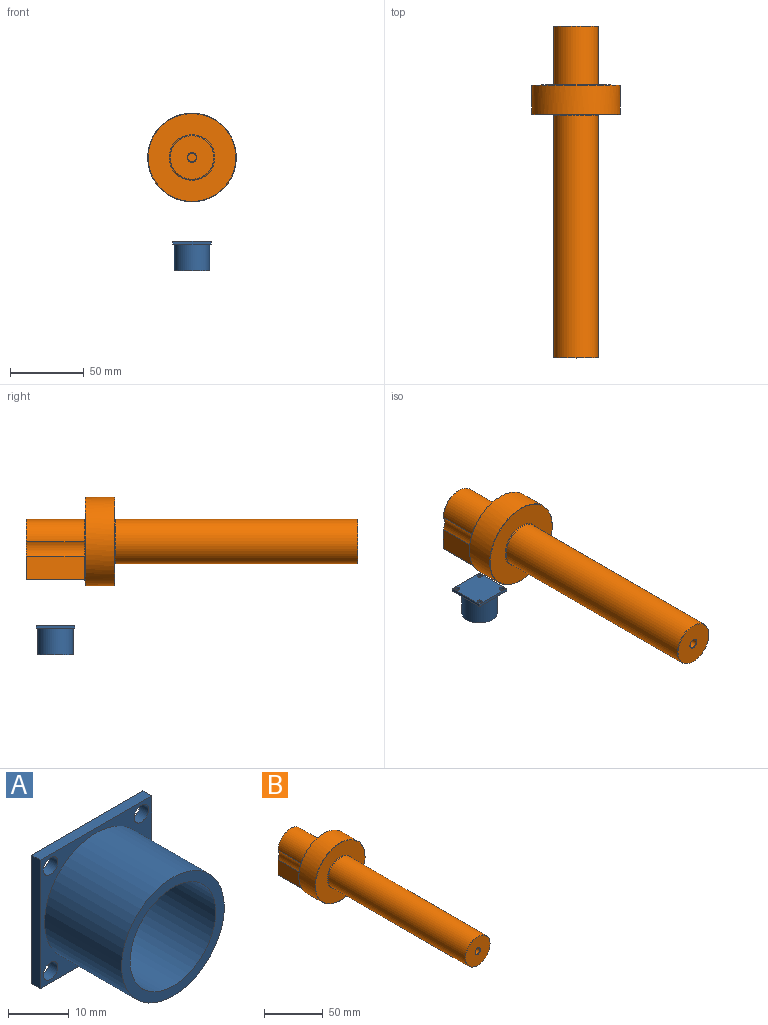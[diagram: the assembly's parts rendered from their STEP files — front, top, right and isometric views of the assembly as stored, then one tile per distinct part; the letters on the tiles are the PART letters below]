
ASSEMBLY  parts=2 mates=1
PART A: 14 faces, bbox 26x20x26 mm
  f0: cylinder r=10mm len=20mm, axis (0,1,0), area 1131mm2, adj f2,f3
  f1: cylinder r=12mm len=24mm, axis (0,1,0), area 1357.2mm2, adj f2,f12
  f2: plane 24x24mm, normal (0,-1,0), area 138.2mm2, adj f0,f1
  f3: plane 20x20mm, normal (0,-1,0), area 314.2mm2, adj f0
  f4: plane 26x2mm, normal (0,0,-1), area 52mm2, adj f5,f11,f12,f13
  f5: plane 26x2mm, normal (1,0,0), area 52mm2, adj f4,f6,f12,f13
  f6: plane 26x2mm, normal (0,0,1), area 52mm2, adj f5,f11,f12,f13
  f7: cylinder r=1.7mm len=3.4mm, axis (0,-1,0), area 21.4mm2, adj f12,f13
  f8: cylinder r=1.7mm len=3.4mm, axis (0,-1,0), area 21.4mm2, adj f12,f13
  f9: cylinder r=1.7mm len=3.4mm, axis (0,-1,0), area 21.4mm2, adj f12,f13
  f10: cylinder r=1.7mm len=3.4mm, axis (0,-1,0), area 21.4mm2, adj f12,f13
  f11: plane 26x2mm, normal (-1,0,0), area 52mm2, adj f4,f6,f12,f13
  f12: plane 26x26mm, normal (0,-1,0), area 187.3mm2, adj f1,f4,f5,f6,f7,f8,f9,f10
  f13: plane 26x26mm, normal (0,1,0), area 639.7mm2, adj f4,f5,f6,f7,f8,f9,f10,f11
PART B: 51 faces, bbox 60x225x60 mm
  f0: cone r=0mm half-angle=59deg, axis (0,0,-1), area 9.4mm2, adj f1
  f1: cylinder r=1.6mm len=10mm, axis (0,0,-1), area 100.5mm2, adj f0,f12
  f2: cone r=0mm half-angle=59deg, axis (0,0,-1), area 9.4mm2, adj f3
  f3: cylinder r=1.6mm len=10mm, axis (0,0,-1), area 100.5mm2, adj f2,f12
  f4: cone r=0mm half-angle=59deg, axis (0,0,-1), area 9.4mm2, adj f5
  f5: cylinder r=1.6mm len=10mm, axis (0,0,-1), area 100.5mm2, adj f4,f12
  f6: cone r=30mm half-angle=45deg, axis (0,-1,0), area 66.8mm2, adj f8,f12,f13,f15,f16,f19,f32,f40
  f7: cylinder r=10mm len=219.75mm, axis (0,1,0), area 13407.3mm2, adj f20,f21,f41
  f8: cylinder r=30mm len=60mm, axis (0,-1,0), area 3675.7mm2, adj f6,f27
  f9: plane 40.48x29.5mm, normal (0,1,0), area 752.4mm2, adj f31,f33,f34,f36,f37,f38,f41
  f10: cylinder r=15mm len=164.25mm, axis (0,1,0), area 15480.2mm2, adj f29,f42
  f11: plane 59.5x59.5mm, normal (0,-1,0), area 2025.7mm2, adj f27,f42
  f12: plane 39.9x29.52mm, normal (0,0,-1), area 796.5mm2, adj f1,f3,f5,f6,f30,f32,f37,f40
  f13: plane 27.12x3.27mm, normal (0,1,0), area 59.8mm2, adj f6,f43
  f14: cylinder r=10mm len=39.25mm, axis (0,1,0), area 411mm2, adj f15,f18,f36,f45
  f15: plane 39.79x15.73mm, normal (-1,0,0), area 617.6mm2, adj f6,f14,f38,f40,f44
  f16: plane 39.79x15.73mm, normal (1,0,0), area 617.6mm2, adj f6,f17,f32,f33,f47
  f17: cylinder r=10mm len=39.25mm, axis (0,1,0), area 411mm2, adj f16,f18,f31,f48
  f18: cylinder r=15mm len=39.25mm, axis (0,1,0), area 1849.6mm2, adj f14,f17,f34,f46
  f19: plane 59.5x55.14mm, normal (0,1,0), area 1542.1mm2, adj f6,f44,f45,f46,f47,f48
  f20: cylinder r=10mm len=25.73mm, axis (0,0,-1), area 1216.7mm2, adj f7,f30
  f21: plane 20x20mm, normal (0,1,0), area 263.9mm2, adj f7,f25
  f22: cylinder r=3mm len=6mm, axis (0,1,0), area 89.5mm2, adj f24,f28
  f23: plane 29.5x29.5mm, normal (0,-1,0), area 650.3mm2, adj f28,f29
  f24: plane 6x6mm, normal (0,-1,0), area 28.3mm2, adj f22
  f25: cylinder r=4mm len=160mm, axis (0,1,0), area 4021.2mm2, adj f21,f26
  f26: plane 8x8mm, normal (0,1,0), area 50.3mm2, adj f25
  f27: cone r=29.75mm half-angle=45deg, axis (0,1,0), area 66.4mm2, adj f8,f11
  f28: cone r=3mm half-angle=45deg, axis (0,-1,0), area 6.9mm2, adj f22,f23
  f29: cone r=14.75mm half-angle=45deg, axis (0,1,0), area 33mm2, adj f10,f23
  f30: cone r=10mm half-angle=45deg, axis (0,0,-1), area 22.5mm2, adj f12,f20
  f31: cone r=10.25mm half-angle=45deg, axis (0,1,0), area 3.7mm2, adj f9,f17,f33,f34
  f32: plane 39.88x0.25mm, normal (0.71,0,-0.71), area 14.1mm2, adj f6,f12,f16,f35
  f33: plane 15.73x0.25mm, normal (0.71,0.71,0), area 5.5mm2, adj f9,f16,f31,f35
  f34: cone r=15mm half-angle=45deg, axis (0,-1,0), area 16.5mm2, adj f9,f18,f31,f36
  f35: plane 0.25x0.25mm, normal (0.58,0.58,-0.58), area 0.1mm2, adj f32,f33,f37
  f36: cone r=10mm half-angle=45deg, axis (0,1,0), area 3.7mm2, adj f9,f14,f34,f38
  f37: plane 29.5x0.25mm, normal (0,0.71,-0.71), area 10.4mm2, adj f9,f12,f35,f39
  f38: plane 15.73x0.25mm, normal (-0.71,0.71,0), area 5.5mm2, adj f9,f15,f36,f39
  f39: plane 0.25x0.25mm, normal (-0.58,0.58,-0.58), area 0.1mm2, adj f37,f38,f40
  f40: plane 39.88x0.25mm, normal (-0.71,0,-0.71), area 14.1mm2, adj f6,f12,f15,f39
  f41: cone r=10.25mm half-angle=45deg, axis (0,1,0), area 22.5mm2, adj f7,f9
  f42: torus R=15.5mm, axis (0,-1,0), area 74.9mm2, adj f10,f11
  f43: cylinder r=0.5mm len=27.84mm, axis (1,0,0), area 21.6mm2, adj f6,f12,f13
  f44: cylinder r=0.5mm len=15.6mm, axis (0,0,-1), area 12.1mm2, adj f6,f15,f19,f45
  f45: torus R=9.5mm, axis (0,1,0), area 8.2mm2, adj f14,f19,f44,f46
  f46: torus R=15.5mm, axis (0,1,0), area 37.6mm2, adj f18,f19,f45,f48
  f47: cylinder r=0.5mm len=15.6mm, axis (0,0,1), area 12.1mm2, adj f6,f16,f19,f48
  f48: torus R=9.5mm, axis (0,1,0), area 8.2mm2, adj f17,f19,f46,f47
  f49: cone r=0mm half-angle=59deg, axis (0,0,-1), area 9.4mm2, adj f50
  f50: cylinder r=1.6mm len=10mm, axis (0,0,-1), area 100.5mm2, adj f12,f49
PLACE A rot(axis=(1,0,0),90deg) t=(88.17,112.32,-67.59)mm
PLACE B t=(88.17,72.35,-8.84)mm fixed
MATE slider B.f49 <-> A.f7  axis (0,0,-1) through (98.78,101.71,-34.82)mm
